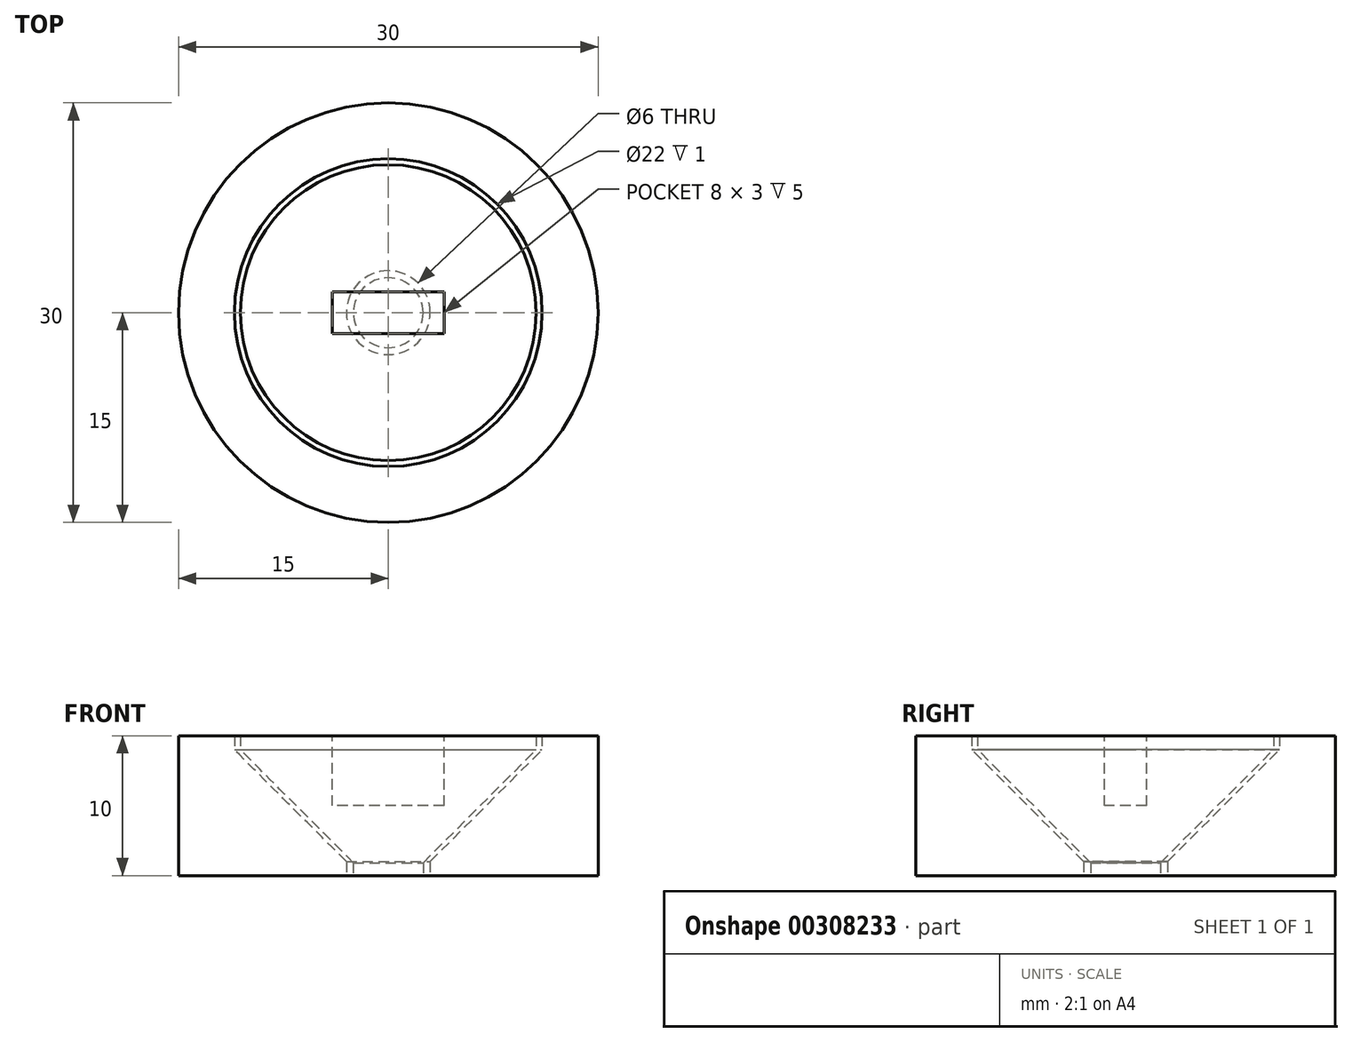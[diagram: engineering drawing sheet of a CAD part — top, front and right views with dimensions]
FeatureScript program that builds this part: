
annotation { "Feature Type Name" : "Feature", "Feature Type Description" : "" }
export const myFeature = defineFeature(function(context is Context, id is Id, definition is map)
    precondition{}
    {
        {
            var Q0;
            Q0=qCreatedBy(makeId("Front.planeOp"),FACE);
            var sketch = newSketch(context, id + "F0", { "sketchPlane" : qUnion([Q0])});
            skLineSegment(sketch, "E0", {"start": v(0, 0) * mm, "end": v(0, 10) * mm});
            skLineSegment(sketch, "E1", {"start": v(0, 10) * mm, "end": v(10.58, 10) * mm});
            skLineSegment(sketch, "E2", {"start": v(10.58, 10) * mm, "end": v(10.58, 9) * mm});
            skLineSegment(sketch, "E3", {"start": v(10.58, 9) * mm, "end": v(2.5, 0.92) * mm});
            skLineSegment(sketch, "E4", {"start": v(2.5, 0.92) * mm, "end": v(2.5, 0) * mm});
            skLineSegment(sketch, "E5", {"start": v(2.5, 0) * mm, "end": v(0, 0) * mm});
            skLineSegment(sketch, "E6", {"start": v(3, 0) * mm, "end": v(3, 1) * mm});
            skLineSegment(sketch, "E7", {"start": v(3, 1) * mm, "end": v(11, 9) * mm});
            skLineSegment(sketch, "E8", {"start": v(11, 9) * mm, "end": v(11, 10) * mm});
            skLineSegment(sketch, "E9", {"start": v(11, 10) * mm, "end": v(15, 10) * mm});
            skLineSegment(sketch, "E10", {"start": v(15, 10) * mm, "end": v(15, 0) * mm});
            skLineSegment(sketch, "E11", {"start": v(15, 0) * mm, "end": v(3, 0) * mm});
            skSolve(sketch);
        }
        {
            var Q0;
            Q0=makeQuery(id+"F0.imprint","IMPRINT",FACE,{"disambiguationData":[TD([[makeQuery(id+"F0.imprint","IMPRINT",EDGE,{"derivedFrom":sQuery(id+"F0.wireOp",EDGE,"E0")}),-1.0]])]});
            var Q1;
            Q1=makeQuery(id+"F0.imprint","IMPRINT",FACE,{"disambiguationData":[TD([[makeQuery(id+"F0.imprint","IMPRINT",EDGE,{"derivedFrom":sQuery(id+"F0.wireOp",EDGE,"E6")}),-1.0]])]});
            var Q2;
            Q2=sQuery(id+"F0.wireOp",EDGE,"E0");
            revolve(context, id + "F1", {"surfaceOperationType" : NewSurfaceOperationType.NEW, "entities" : qUnion([Q0, Q1]), "axis" : qUnion([Q2]), "revolveType" : RevolveType.FULL});
        }
        {
            var Q0;
            Q0=makeQuery(id+"F1.opRevolve","SWEPT_FACE",FACE,{"disambiguationData":[OSD([sQuery(id+"F0.wireOp",EDGE,"E1")])]});
            var sketch = newSketch(context, id + "F2", { "sketchPlane" : qUnion([Q0])});
            skLineSegment(sketch, "E12.bottom", {"start": v(4, 1.5) * mm, "end": v(-4, 1.5) * mm});
            skLineSegment(sketch, "E12.top", {"start": v(4, -1.5) * mm, "end": v(-4, -1.5) * mm});
            skLineSegment(sketch, "E12.left", {"start": v(4, 1.5) * mm, "end": v(4, -1.5) * mm});
            skLineSegment(sketch, "E12.right", {"start": v(-4, 1.5) * mm, "end": v(-4, -1.5) * mm});
            skPoint(sketch, "E12.middle", {"position": v(0, 0) * mm});
            skSolve(sketch);
        }
        {
            var Q0;
            Q0=makeQuery(id+"F2.imprint","IMPRINT",FACE,{"disambiguationData":[TD([[makeQuery(id+"F2.imprint","IMPRINT",EDGE,{"derivedFrom":sQuery(id+"F2.wireOp",EDGE,"E12.bottom")}),1.0]])]});
            extrude(context, id + "F3", {"entities" : qUnion([Q0]), "operationType" : NewBodyOperationType.REMOVE, "oppositeDirection" : true, "depth" : 5 * mm, "offsetDistance" : 25 * mm});
        }
    });
